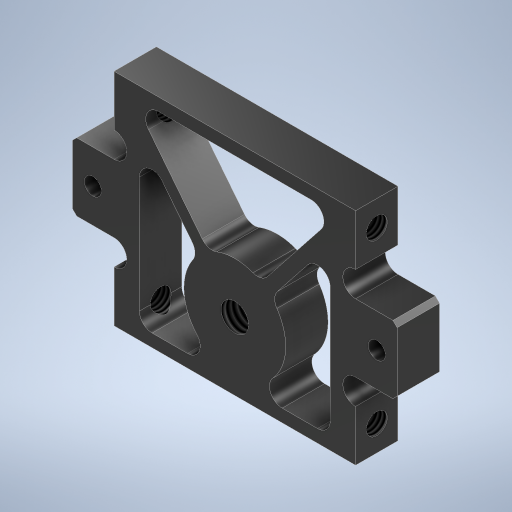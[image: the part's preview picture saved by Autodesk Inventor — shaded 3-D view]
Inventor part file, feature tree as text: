
AUTODESK INVENTOR PART (.ipt)
format: ipt  version: 2024.2 (Build 282272000, 272)  size: 409,600 bytes
history: native  units: mm
features: sketch x2, hole x2, extrude x1, mirror x1
ambient origin geometry x8: Origin, YZ Plane, XZ Plane, XY Plane, X Axis, Y Axis, Z Axis, Center Point
bodies: Solid1 (feature_tree)
feature tree (6):
  sketch  "Sketch1"  dims[d6=9.0mm d7=1.5mm]
  extrude  "Extrusion1"  Depth=1.5mm
  hole  "Side-M3"  [1 undecoded]
  hole  "Phi2-H7"  [1 undecoded]
  mirror  "Mirror1"
  sketch  "Sketch2"  dims[d8=8.0mm d9=4.9mm d10=28.5mm d15=6.0mm d18=9.0mm d19=6.0mm d20=6.0mm d21=5.0mm d22=0.0mm d23=3.242mm d24=8.0mm d25=4.0mm d26=2.0mm d27=90.0deg d28=8.0mm d29=20.594885mm d30=2.459mm d31=6.0mm d32=4.0mm d33=2.0mm d34=90.0deg d35=6.0mm d36=0.0mm d37=0.5mm d38=2.0mm d39=45.0deg d53=2.0mm d54=6.0mm d55=4.0mm d56=2.0mm d57=90.0deg d58=5.0mm d59=0.0mm d60=12.0mm d62=1.5mm d66=1.5mm d74=1.5mm d77=18.0mm d78=2.5mm d79=3.0mm]
note: 2 required parameter values undecoded (feature->parameter linkage not recoverable at this tier; creation-order binding heuristic only, values carry confidence <= 0.55)
